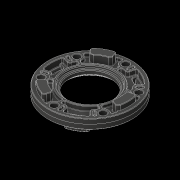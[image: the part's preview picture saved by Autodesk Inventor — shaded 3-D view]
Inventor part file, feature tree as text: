
AUTODESK INVENTOR PART (.ipt)
format: ipt  version: 2016 (Build 200138000, 138)  size: 2,391,552 bytes
history: native  units: in
note: dims shown in document units (in); Inventor stores cm internally (conversion verified against a paired STEP export)
features: fillet x1
ambient origin geometry x8: Origin, YZ Plane, XZ Plane, XY Plane, X Axis, Y Axis, Z Axis, Center Point
bodies: Solid1 (feature_tree)
feature tree (1):
  fillet  "Fillet10"  [1 undecoded]
note: 1 required parameter value undecoded (feature->parameter linkage not recoverable at this tier; creation-order binding heuristic only, values carry confidence <= 0.55)
